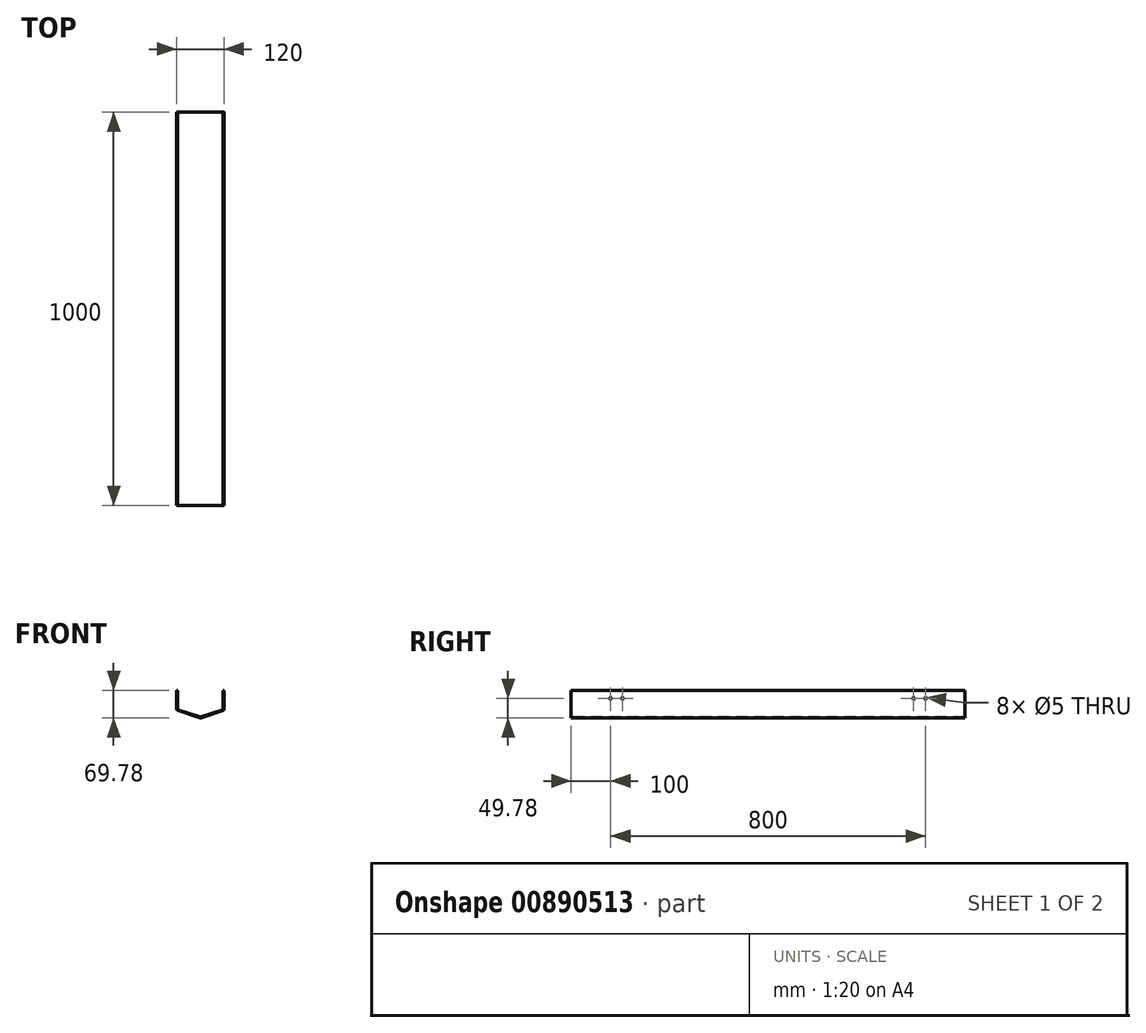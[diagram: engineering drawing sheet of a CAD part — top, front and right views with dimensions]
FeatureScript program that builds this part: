
annotation { "Feature Type Name" : "Feature", "Feature Type Description" : "" }
export const myFeature = defineFeature(function(context is Context, id is Id, definition is map)
    precondition{}
    {
        {
            var Q0;
            Q0=qCreatedBy(makeId("Front.planeOp"),FACE);
            var sketch = newSketch(context, id + "F0", { "sketchPlane" : qUnion([Q0])});
            skLineSegment(sketch, "E0", {"start": v(0, 70) * mm, "end": v(0, 2.1) * mm});
            skLineSegment(sketch, "E1", {"start": v(0, 0) * mm, "end": v(60, 20) * mm});
            skLineSegment(sketch, "E2", {"start": v(60, 20) * mm, "end": v(0, 0) * mm});
            skLineSegment(sketch, "E3", {"start": v(-60, 20) * mm, "end": v(0, 0) * mm});
            skLineSegment(sketch, "E4", {"start": v(60, 20) * mm, "end": v(60, 70) * mm});
            skLineSegment(sketch, "E5", {"start": v(-60, 20) * mm, "end": v(-60, 70) * mm});
            skLineSegment(sketch, "E6", {"start": v(-60, 70) * mm, "end": v(-58, 70) * mm});
            skLineSegment(sketch, "E7.0", {"start": v(-58, 21.44) * mm, "end": v(-58, 70) * mm});
            skLineSegment(sketch, "E7.1", {"start": v(-58, 21.44) * mm, "end": v(0, 2.1) * mm});
            skLineSegment(sketch, "E7.2", {"start": v(0, 2.1) * mm, "end": v(58, 21.44) * mm});
            skLineSegment(sketch, "E7.3", {"start": v(58, 21.44) * mm, "end": v(58, 70) * mm});
            skLineSegment(sketch, "E8.trimOffspring", {"start": v(58, 70) * mm, "end": v(60, 70) * mm});
            skSolve(sketch);
        }
        {
            var Q0;
            Q0 = qSketchRegion(id + "F0", true);
            extrude(context, id + "F1", {"entities" : qUnion([Q0]), "depth" : 1000 * mm, "offsetDistance" : 25.4 * mm});
        }
        {
            var Q0;
            Q0=makeQuery(id+"F1.opExtrude","SWEPT_EDGE",EDGE,{"disambiguationData":[OSD([sQuery(id+"F0.wireOp",EDGE,"E2"),sQuery(id+"F0.wireOp",EDGE,"E4")])]});
            var Q1;
            Q1=makeQuery(id+"F1.opExtrude","SWEPT_EDGE",EDGE,{"disambiguationData":[OSD([sQuery(id+"F0.wireOp",EDGE,"E2"),sQuery(id+"F0.wireOp",EDGE,"E3")])]});
            var Q2;
            Q2=makeQuery(id+"F1.opExtrude","SWEPT_EDGE",EDGE,{"disambiguationData":[OSD([sQuery(id+"F0.wireOp",EDGE,"E3"),sQuery(id+"F0.wireOp",EDGE,"E5")])]});
            fillet(context, id + "F2", {"entities" : qUnion([Q0, Q1, Q2]), "radius" : 4 * mm, "tangentPropagation" : true, "allowEdgeOverflow" : false});
        }
        {
            var Q0;
            Q0=makeQuery(id+"F1.opExtrude","SWEPT_EDGE",EDGE,{"disambiguationData":[OSD([sQuery(id+"F0.wireOp",EDGE,"E7.0"),sQuery(id+"F0.wireOp",EDGE,"E7.1")])]});
            var Q1;
            Q1=makeQuery(id+"F1.opExtrude","SWEPT_EDGE",EDGE,{"disambiguationData":[OSD([sQuery(id+"F0.wireOp",EDGE,"E7.1"),sQuery(id+"F0.wireOp",EDGE,"E7.2")])]});
            var Q2;
            Q2=makeQuery(id+"F1.opExtrude","SWEPT_EDGE",EDGE,{"disambiguationData":[OSD([sQuery(id+"F0.wireOp",EDGE,"E7.2"),sQuery(id+"F0.wireOp",EDGE,"E7.3")])]});
            fillet(context, id + "F3", {"entities" : qUnion([Q0, Q1, Q2]), "radius" : 2 * mm, "tangentPropagation" : true, "allowEdgeOverflow" : false});
        }
        {
            var Q0;
            Q0=makeQuery(id+"F1.opExtrude","SWEPT_FACE",FACE,{"disambiguationData":[OSD([sQuery(id+"F0.wireOp",EDGE,"E5")])]});
            var sketch = newSketch(context, id + "F4", { "sketchPlane" : qUnion([Q0])});
            skLineSegment(sketch, "E9", {"start": v(100, 50) * mm, "end": v(130, 50) * mm});
            skLineSegment(sketch, "E10", {"start": v(870, 50) * mm, "end": v(900, 50) * mm});
            skLineSegment(sketch, "E11", {"start": v(900, 50) * mm, "end": v(870, 50) * mm});
            skSolve(sketch);
        }
        {
            var Q0;
            Q0=sQuery(id+"F4.wireOp",VERTEX,"E9.start");
            var Q1;
            Q1=sQuery(id+"F4.wireOp",VERTEX,"E9.end");
            var Q2;
            Q2=sQuery(id+"F4.wireOp",VERTEX,"E10.start");
            var Q3;
            Q3=sQuery(id+"F4.wireOp",VERTEX,"E11.start");
            var Q4;
            Q4=makeQuery(id+"F1.opExtrude","SWEPT_BODY",BODY,{"disambiguationData":[OSD([sQuery(id+"F0.wireOp",EDGE,"E2"),sQuery(id+"F0.wireOp",EDGE,"E3"),sQuery(id+"F0.wireOp",EDGE,"E4"),sQuery(id+"F0.wireOp",EDGE,"E5"),sQuery(id+"F0.wireOp",EDGE,"E6"),sQuery(id+"F0.wireOp",EDGE,"E7.0"),sQuery(id+"F0.wireOp",EDGE,"E7.1"),sQuery(id+"F0.wireOp",EDGE,"E7.2"),sQuery(id+"F0.wireOp",EDGE,"E7.3"),sQuery(id+"F0.wireOp",EDGE,"E8.trimOffspring")])]});
            hole(context, id + "F5", {"style" : HoleStyle.SIMPLE, "endStyle" : HoleEndStyle.THROUGH, "holeDiameter" : 5 * mm, "majorDiameter" : 6.35 * mm, "isTappedThrough" : true, "tappedDepth" : 12.7 * mm, "tapClearance" : 3, "locations" : qUnion([Q0, Q1, Q2, Q3]), "scope" : qUnion([Q4])});
        }
    });
